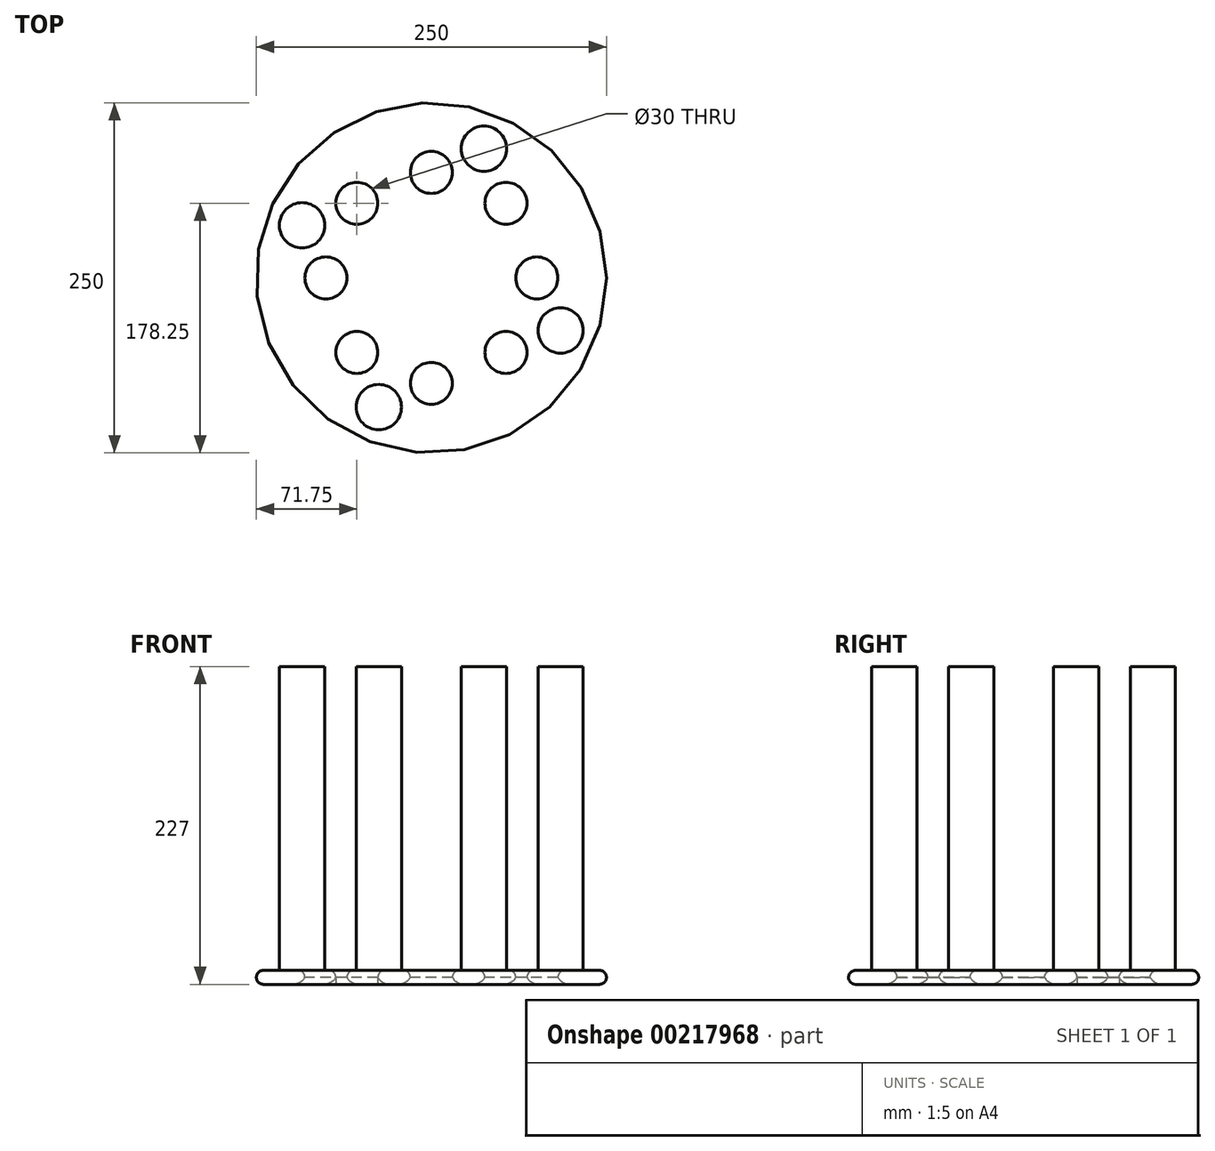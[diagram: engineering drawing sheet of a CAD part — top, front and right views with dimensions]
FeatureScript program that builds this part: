
annotation { "Feature Type Name" : "Feature", "Feature Type Description" : "" }
export const myFeature = defineFeature(function(context is Context, id is Id, definition is map)
    precondition{}
    {
        {
            var Q0;
            Q0=qCreatedBy(makeId("Top.planeOp"),FACE);
            var sketch = newSketch(context, id + "F0", { "sketchPlane" : qUnion([Q0])});
            skCircle(sketch, "E0", {"center": v(0, 0) * mm, "radius": 125 * mm});
            skCircle(sketch, "E1", {"center": v(0, 75.3) * mm, "radius": 15 * mm});
            skCircle(sketch, "E2.1.0", {"center": v(-53.25, 53.25) * mm, "radius": 15 * mm});
            skCircle(sketch, "E2.2.0", {"center": v(-75.3, 0) * mm, "radius": 15 * mm});
            skCircle(sketch, "E2.3.0", {"center": v(-53.25, -53.25) * mm, "radius": 15 * mm});
            skCircle(sketch, "E2.4.0", {"center": v(0, -75.3) * mm, "radius": 15 * mm});
            skCircle(sketch, "E2.5.0", {"center": v(53.25, -53.25) * mm, "radius": 15 * mm});
            skCircle(sketch, "E2.6.0", {"center": v(75.3, 0) * mm, "radius": 15 * mm});
            skCircle(sketch, "E2.7.0", {"center": v(53.25, 53.25) * mm, "radius": 15 * mm});
            skSolve(sketch);
        }
        {
            var Q0;
            Q0=makeQuery(id+"F0.imprint","IMPRINT",FACE,{"disambiguationData":[TD([[makeQuery(id+"F0.imprint","IMPRINT",EDGE,{"derivedFrom":sQuery(id+"F0.wireOp",EDGE,"E0")}),1.0]])]});
            extrude(context, id + "F1", {"entities" : qUnion([Q0]), "depth" : 10 * mm});
        }
        {
            var Q0;
            Q0=makeQuery(id+"F1.opExtrude","CAP_FACE",FACE,{"disambiguationData":[OSD([sQuery(id+"F0.wireOp",EDGE,"E0"),sQuery(id+"F0.wireOp",EDGE,"E1"),sQuery(id+"F0.wireOp",EDGE,"E2.1.0"),sQuery(id+"F0.wireOp",EDGE,"E2.2.0"),sQuery(id+"F0.wireOp",EDGE,"E2.3.0"),sQuery(id+"F0.wireOp",EDGE,"E2.4.0"),sQuery(id+"F0.wireOp",EDGE,"E2.5.0"),sQuery(id+"F0.wireOp",EDGE,"E2.6.0"),sQuery(id+"F0.wireOp",EDGE,"E2.7.0")])],"isStart":false});
            var Q1;
            Q1=makeQuery(id+"F1.opExtrude","SWEPT_FACE",FACE,{"disambiguationData":[OSD([sQuery(id+"F0.wireOp",EDGE,"E0")])]});
            fillet(context, id + "F2", {"entities" : qUnion([Q0, Q1]), "radius" : 5 * mm, "tangentPropagation" : true, "allowEdgeOverflow" : false});
        }
        {
            var Q0;
            {var subQ0=sQuery(id+"F0.wireOp",EDGE,"E0");Q0=makeQuery(id+"F2.opFillet","BLEND_EDGE",EDGE,{"blendedFrom":[makeQuery(id+"F1.opExtrude","CAP_EDGE",EDGE,{"disambiguationData":[OSD([subQ0])],"isStart":true}),makeQuery(id+"F1.opExtrude","CAP_FACE",FACE,{"disambiguationData":[OSD([subQ0,sQuery(id+"F0.wireOp",EDGE,"E1"),sQuery(id+"F0.wireOp",EDGE,"E2.1.0"),sQuery(id+"F0.wireOp",EDGE,"E2.2.0"),sQuery(id+"F0.wireOp",EDGE,"E2.3.0"),sQuery(id+"F0.wireOp",EDGE,"E2.4.0"),sQuery(id+"F0.wireOp",EDGE,"E2.5.0"),sQuery(id+"F0.wireOp",EDGE,"E2.6.0"),sQuery(id+"F0.wireOp",EDGE,"E2.7.0")])],"isStart":true})],"blendedInto":[makeQuery(id+"F1.opExtrude","CAP_FACE",FACE,{"disambiguationData":[OSD([subQ0,sQuery(id+"F0.wireOp",EDGE,"E1"),sQuery(id+"F0.wireOp",EDGE,"E2.1.0"),sQuery(id+"F0.wireOp",EDGE,"E2.2.0"),sQuery(id+"F0.wireOp",EDGE,"E2.3.0"),sQuery(id+"F0.wireOp",EDGE,"E2.4.0"),sQuery(id+"F0.wireOp",EDGE,"E2.5.0"),sQuery(id+"F0.wireOp",EDGE,"E2.6.0"),sQuery(id+"F0.wireOp",EDGE,"E2.7.0")])],"isStart":true})]});}
            var Q1;
            {var subQ0=sQuery(id+"F0.wireOp",EDGE,"E2.1.0");Q1=makeQuery(id+"F2.opFillet","BLEND_EDGE",EDGE,{"blendedFrom":[makeQuery(id+"F1.opExtrude","CAP_EDGE",EDGE,{"disambiguationData":[OSD([subQ0])],"isStart":false}),makeQuery(id+"F1.opExtrude","SWEPT_FACE",FACE,{"disambiguationData":[OSD([subQ0])]})],"blendedInto":[makeQuery(id+"F1.opExtrude","SWEPT_FACE",FACE,{"disambiguationData":[OSD([subQ0])]})]});}
            var Q2;
            Q2=makeQuery(id+"F1.opExtrude","CAP_EDGE",EDGE,{"disambiguationData":[OSD([sQuery(id+"F0.wireOp",EDGE,"E2.2.0")])],"isStart":true});
            var Q3;
            Q3=makeQuery(id+"F1.opExtrude","CAP_EDGE",EDGE,{"disambiguationData":[OSD([sQuery(id+"F0.wireOp",EDGE,"E2.3.0")])],"isStart":true});
            var Q4;
            Q4=makeQuery(id+"F1.opExtrude","CAP_EDGE",EDGE,{"disambiguationData":[OSD([sQuery(id+"F0.wireOp",EDGE,"E2.4.0")])],"isStart":true});
            var Q5;
            {var subQ0=sQuery(id+"F0.wireOp",EDGE,"E2.5.0");Q5=makeQuery(id+"F2.opFillet","BLEND_EDGE",EDGE,{"blendedFrom":[makeQuery(id+"F1.opExtrude","CAP_EDGE",EDGE,{"disambiguationData":[OSD([subQ0])],"isStart":false}),makeQuery(id+"F1.opExtrude","SWEPT_FACE",FACE,{"disambiguationData":[OSD([subQ0])]})],"blendedInto":[makeQuery(id+"F1.opExtrude","SWEPT_FACE",FACE,{"disambiguationData":[OSD([subQ0])]})]});}
            var Q6;
            Q6=makeQuery(id+"F1.opExtrude","CAP_EDGE",EDGE,{"disambiguationData":[OSD([sQuery(id+"F0.wireOp",EDGE,"E2.5.0")])],"isStart":true});
            var Q7;
            Q7=makeQuery(id+"F1.opExtrude","CAP_EDGE",EDGE,{"disambiguationData":[OSD([sQuery(id+"F0.wireOp",EDGE,"E1")])],"isStart":true});
            var Q8;
            Q8=makeQuery(id+"F1.opExtrude","CAP_EDGE",EDGE,{"disambiguationData":[OSD([sQuery(id+"F0.wireOp",EDGE,"E2.7.0")])],"isStart":true});
            var Q9;
            Q9=makeQuery(id+"F1.opExtrude","CAP_EDGE",EDGE,{"disambiguationData":[OSD([sQuery(id+"F0.wireOp",EDGE,"E2.6.0")])],"isStart":true});
            var Q10;
            {var subQ0=sQuery(id+"F0.wireOp",EDGE,"E2.6.0");Q10=makeQuery(id+"F2.opFillet","BLEND_EDGE",EDGE,{"blendedFrom":[makeQuery(id+"F1.opExtrude","CAP_EDGE",EDGE,{"disambiguationData":[OSD([subQ0])],"isStart":false}),makeQuery(id+"F1.opExtrude","CAP_FACE",FACE,{"disambiguationData":[OSD([sQuery(id+"F0.wireOp",EDGE,"E0"),sQuery(id+"F0.wireOp",EDGE,"E1"),sQuery(id+"F0.wireOp",EDGE,"E2.1.0"),sQuery(id+"F0.wireOp",EDGE,"E2.2.0"),sQuery(id+"F0.wireOp",EDGE,"E2.3.0"),sQuery(id+"F0.wireOp",EDGE,"E2.4.0"),sQuery(id+"F0.wireOp",EDGE,"E2.5.0"),subQ0,sQuery(id+"F0.wireOp",EDGE,"E2.7.0")])],"isStart":false})],"blendedInto":[makeQuery(id+"F1.opExtrude","CAP_FACE",FACE,{"disambiguationData":[OSD([sQuery(id+"F0.wireOp",EDGE,"E0"),sQuery(id+"F0.wireOp",EDGE,"E1"),sQuery(id+"F0.wireOp",EDGE,"E2.1.0"),sQuery(id+"F0.wireOp",EDGE,"E2.2.0"),sQuery(id+"F0.wireOp",EDGE,"E2.3.0"),sQuery(id+"F0.wireOp",EDGE,"E2.4.0"),sQuery(id+"F0.wireOp",EDGE,"E2.5.0"),subQ0,sQuery(id+"F0.wireOp",EDGE,"E2.7.0")])],"isStart":false})]});}
            var Q11;
            {var subQ0=sQuery(id+"F0.wireOp",EDGE,"E2.7.0");Q11=makeQuery(id+"F2.opFillet","BLEND_EDGE",EDGE,{"blendedFrom":[makeQuery(id+"F1.opExtrude","CAP_EDGE",EDGE,{"disambiguationData":[OSD([subQ0])],"isStart":false}),makeQuery(id+"F1.opExtrude","CAP_FACE",FACE,{"disambiguationData":[OSD([sQuery(id+"F0.wireOp",EDGE,"E0"),sQuery(id+"F0.wireOp",EDGE,"E1"),sQuery(id+"F0.wireOp",EDGE,"E2.1.0"),sQuery(id+"F0.wireOp",EDGE,"E2.2.0"),sQuery(id+"F0.wireOp",EDGE,"E2.3.0"),sQuery(id+"F0.wireOp",EDGE,"E2.4.0"),sQuery(id+"F0.wireOp",EDGE,"E2.5.0"),sQuery(id+"F0.wireOp",EDGE,"E2.6.0"),subQ0])],"isStart":false})],"blendedInto":[makeQuery(id+"F1.opExtrude","CAP_FACE",FACE,{"disambiguationData":[OSD([sQuery(id+"F0.wireOp",EDGE,"E0"),sQuery(id+"F0.wireOp",EDGE,"E1"),sQuery(id+"F0.wireOp",EDGE,"E2.1.0"),sQuery(id+"F0.wireOp",EDGE,"E2.2.0"),sQuery(id+"F0.wireOp",EDGE,"E2.3.0"),sQuery(id+"F0.wireOp",EDGE,"E2.4.0"),sQuery(id+"F0.wireOp",EDGE,"E2.5.0"),sQuery(id+"F0.wireOp",EDGE,"E2.6.0"),subQ0])],"isStart":false})]});}
            var Q12;
            {var subQ0=sQuery(id+"F0.wireOp",EDGE,"E1");Q12=makeQuery(id+"F2.opFillet","BLEND_EDGE",EDGE,{"blendedFrom":[makeQuery(id+"F1.opExtrude","CAP_EDGE",EDGE,{"disambiguationData":[OSD([subQ0])],"isStart":false}),makeQuery(id+"F1.opExtrude","CAP_FACE",FACE,{"disambiguationData":[OSD([sQuery(id+"F0.wireOp",EDGE,"E0"),subQ0,sQuery(id+"F0.wireOp",EDGE,"E2.1.0"),sQuery(id+"F0.wireOp",EDGE,"E2.2.0"),sQuery(id+"F0.wireOp",EDGE,"E2.3.0"),sQuery(id+"F0.wireOp",EDGE,"E2.4.0"),sQuery(id+"F0.wireOp",EDGE,"E2.5.0"),sQuery(id+"F0.wireOp",EDGE,"E2.6.0"),sQuery(id+"F0.wireOp",EDGE,"E2.7.0")])],"isStart":false})],"blendedInto":[makeQuery(id+"F1.opExtrude","CAP_FACE",FACE,{"disambiguationData":[OSD([sQuery(id+"F0.wireOp",EDGE,"E0"),subQ0,sQuery(id+"F0.wireOp",EDGE,"E2.1.0"),sQuery(id+"F0.wireOp",EDGE,"E2.2.0"),sQuery(id+"F0.wireOp",EDGE,"E2.3.0"),sQuery(id+"F0.wireOp",EDGE,"E2.4.0"),sQuery(id+"F0.wireOp",EDGE,"E2.5.0"),sQuery(id+"F0.wireOp",EDGE,"E2.6.0"),sQuery(id+"F0.wireOp",EDGE,"E2.7.0")])],"isStart":false})]});}
            var Q13;
            {var subQ0=sQuery(id+"F0.wireOp",EDGE,"E2.1.0");Q13=makeQuery(id+"F2.opFillet","BLEND_EDGE",EDGE,{"blendedFrom":[makeQuery(id+"F1.opExtrude","CAP_EDGE",EDGE,{"disambiguationData":[OSD([subQ0])],"isStart":false}),makeQuery(id+"F1.opExtrude","CAP_FACE",FACE,{"disambiguationData":[OSD([sQuery(id+"F0.wireOp",EDGE,"E0"),sQuery(id+"F0.wireOp",EDGE,"E1"),subQ0,sQuery(id+"F0.wireOp",EDGE,"E2.2.0"),sQuery(id+"F0.wireOp",EDGE,"E2.3.0"),sQuery(id+"F0.wireOp",EDGE,"E2.4.0"),sQuery(id+"F0.wireOp",EDGE,"E2.5.0"),sQuery(id+"F0.wireOp",EDGE,"E2.6.0"),sQuery(id+"F0.wireOp",EDGE,"E2.7.0")])],"isStart":false})],"blendedInto":[makeQuery(id+"F1.opExtrude","CAP_FACE",FACE,{"disambiguationData":[OSD([sQuery(id+"F0.wireOp",EDGE,"E0"),sQuery(id+"F0.wireOp",EDGE,"E1"),subQ0,sQuery(id+"F0.wireOp",EDGE,"E2.2.0"),sQuery(id+"F0.wireOp",EDGE,"E2.3.0"),sQuery(id+"F0.wireOp",EDGE,"E2.4.0"),sQuery(id+"F0.wireOp",EDGE,"E2.5.0"),sQuery(id+"F0.wireOp",EDGE,"E2.6.0"),sQuery(id+"F0.wireOp",EDGE,"E2.7.0")])],"isStart":false})]});}
            var Q14;
            {var subQ0=sQuery(id+"F0.wireOp",EDGE,"E2.2.0");Q14=makeQuery(id+"F2.opFillet","BLEND_EDGE",EDGE,{"blendedFrom":[makeQuery(id+"F1.opExtrude","CAP_EDGE",EDGE,{"disambiguationData":[OSD([subQ0])],"isStart":false}),makeQuery(id+"F1.opExtrude","CAP_FACE",FACE,{"disambiguationData":[OSD([sQuery(id+"F0.wireOp",EDGE,"E0"),sQuery(id+"F0.wireOp",EDGE,"E1"),sQuery(id+"F0.wireOp",EDGE,"E2.1.0"),subQ0,sQuery(id+"F0.wireOp",EDGE,"E2.3.0"),sQuery(id+"F0.wireOp",EDGE,"E2.4.0"),sQuery(id+"F0.wireOp",EDGE,"E2.5.0"),sQuery(id+"F0.wireOp",EDGE,"E2.6.0"),sQuery(id+"F0.wireOp",EDGE,"E2.7.0")])],"isStart":false})],"blendedInto":[makeQuery(id+"F1.opExtrude","CAP_FACE",FACE,{"disambiguationData":[OSD([sQuery(id+"F0.wireOp",EDGE,"E0"),sQuery(id+"F0.wireOp",EDGE,"E1"),sQuery(id+"F0.wireOp",EDGE,"E2.1.0"),subQ0,sQuery(id+"F0.wireOp",EDGE,"E2.3.0"),sQuery(id+"F0.wireOp",EDGE,"E2.4.0"),sQuery(id+"F0.wireOp",EDGE,"E2.5.0"),sQuery(id+"F0.wireOp",EDGE,"E2.6.0"),sQuery(id+"F0.wireOp",EDGE,"E2.7.0")])],"isStart":false})]});}
            var Q15;
            {var subQ0=sQuery(id+"F0.wireOp",EDGE,"E2.3.0");Q15=makeQuery(id+"F2.opFillet","BLEND_EDGE",EDGE,{"blendedFrom":[makeQuery(id+"F1.opExtrude","CAP_EDGE",EDGE,{"disambiguationData":[OSD([subQ0])],"isStart":false}),makeQuery(id+"F1.opExtrude","SWEPT_FACE",FACE,{"disambiguationData":[OSD([subQ0])]})],"blendedInto":[makeQuery(id+"F1.opExtrude","SWEPT_FACE",FACE,{"disambiguationData":[OSD([subQ0])]})]});}
            var Q16;
            {var subQ0=sQuery(id+"F0.wireOp",EDGE,"E2.3.0");Q16=makeQuery(id+"F2.opFillet","BLEND_EDGE",EDGE,{"blendedFrom":[makeQuery(id+"F1.opExtrude","CAP_EDGE",EDGE,{"disambiguationData":[OSD([subQ0])],"isStart":false}),makeQuery(id+"F1.opExtrude","CAP_FACE",FACE,{"disambiguationData":[OSD([sQuery(id+"F0.wireOp",EDGE,"E0"),sQuery(id+"F0.wireOp",EDGE,"E1"),sQuery(id+"F0.wireOp",EDGE,"E2.1.0"),sQuery(id+"F0.wireOp",EDGE,"E2.2.0"),subQ0,sQuery(id+"F0.wireOp",EDGE,"E2.4.0"),sQuery(id+"F0.wireOp",EDGE,"E2.5.0"),sQuery(id+"F0.wireOp",EDGE,"E2.6.0"),sQuery(id+"F0.wireOp",EDGE,"E2.7.0")])],"isStart":false})],"blendedInto":[makeQuery(id+"F1.opExtrude","CAP_FACE",FACE,{"disambiguationData":[OSD([sQuery(id+"F0.wireOp",EDGE,"E0"),sQuery(id+"F0.wireOp",EDGE,"E1"),sQuery(id+"F0.wireOp",EDGE,"E2.1.0"),sQuery(id+"F0.wireOp",EDGE,"E2.2.0"),subQ0,sQuery(id+"F0.wireOp",EDGE,"E2.4.0"),sQuery(id+"F0.wireOp",EDGE,"E2.5.0"),sQuery(id+"F0.wireOp",EDGE,"E2.6.0"),sQuery(id+"F0.wireOp",EDGE,"E2.7.0")])],"isStart":false})]});}
            var Q17;
            {var subQ0=sQuery(id+"F0.wireOp",EDGE,"E2.4.0");Q17=makeQuery(id+"F2.opFillet","BLEND_EDGE",EDGE,{"blendedFrom":[makeQuery(id+"F1.opExtrude","CAP_EDGE",EDGE,{"disambiguationData":[OSD([subQ0])],"isStart":false}),makeQuery(id+"F1.opExtrude","CAP_FACE",FACE,{"disambiguationData":[OSD([sQuery(id+"F0.wireOp",EDGE,"E0"),sQuery(id+"F0.wireOp",EDGE,"E1"),sQuery(id+"F0.wireOp",EDGE,"E2.1.0"),sQuery(id+"F0.wireOp",EDGE,"E2.2.0"),sQuery(id+"F0.wireOp",EDGE,"E2.3.0"),subQ0,sQuery(id+"F0.wireOp",EDGE,"E2.5.0"),sQuery(id+"F0.wireOp",EDGE,"E2.6.0"),sQuery(id+"F0.wireOp",EDGE,"E2.7.0")])],"isStart":false})],"blendedInto":[makeQuery(id+"F1.opExtrude","CAP_FACE",FACE,{"disambiguationData":[OSD([sQuery(id+"F0.wireOp",EDGE,"E0"),sQuery(id+"F0.wireOp",EDGE,"E1"),sQuery(id+"F0.wireOp",EDGE,"E2.1.0"),sQuery(id+"F0.wireOp",EDGE,"E2.2.0"),sQuery(id+"F0.wireOp",EDGE,"E2.3.0"),subQ0,sQuery(id+"F0.wireOp",EDGE,"E2.5.0"),sQuery(id+"F0.wireOp",EDGE,"E2.6.0"),sQuery(id+"F0.wireOp",EDGE,"E2.7.0")])],"isStart":false})]});}
            var Q18;
            {var subQ0=sQuery(id+"F0.wireOp",EDGE,"E2.5.0");Q18=makeQuery(id+"F2.opFillet","BLEND_EDGE",EDGE,{"blendedFrom":[makeQuery(id+"F1.opExtrude","CAP_EDGE",EDGE,{"disambiguationData":[OSD([subQ0])],"isStart":false}),makeQuery(id+"F1.opExtrude","CAP_FACE",FACE,{"disambiguationData":[OSD([sQuery(id+"F0.wireOp",EDGE,"E0"),sQuery(id+"F0.wireOp",EDGE,"E1"),sQuery(id+"F0.wireOp",EDGE,"E2.1.0"),sQuery(id+"F0.wireOp",EDGE,"E2.2.0"),sQuery(id+"F0.wireOp",EDGE,"E2.3.0"),sQuery(id+"F0.wireOp",EDGE,"E2.4.0"),subQ0,sQuery(id+"F0.wireOp",EDGE,"E2.6.0"),sQuery(id+"F0.wireOp",EDGE,"E2.7.0")])],"isStart":false})],"blendedInto":[makeQuery(id+"F1.opExtrude","CAP_FACE",FACE,{"disambiguationData":[OSD([sQuery(id+"F0.wireOp",EDGE,"E0"),sQuery(id+"F0.wireOp",EDGE,"E1"),sQuery(id+"F0.wireOp",EDGE,"E2.1.0"),sQuery(id+"F0.wireOp",EDGE,"E2.2.0"),sQuery(id+"F0.wireOp",EDGE,"E2.3.0"),sQuery(id+"F0.wireOp",EDGE,"E2.4.0"),subQ0,sQuery(id+"F0.wireOp",EDGE,"E2.6.0"),sQuery(id+"F0.wireOp",EDGE,"E2.7.0")])],"isStart":false})]});}
            fillet(context, id + "F3", {"entities" : qUnion([Q0, Q1, Q2, Q3, Q4, Q5, Q6, Q7, Q8, Q9, Q10, Q11, Q12, Q13, Q14, Q15, Q16, Q17, Q18]), "radius" : 10 * mm, "tangentPropagation" : true, "allowEdgeOverflow" : false});
        }
        {
            var Q0;
            Q0=makeQuery(id+"F1.opExtrude","CAP_FACE",FACE,{"disambiguationData":[OSD([sQuery(id+"F0.wireOp",EDGE,"E0"),sQuery(id+"F0.wireOp",EDGE,"E1"),sQuery(id+"F0.wireOp",EDGE,"E2.1.0"),sQuery(id+"F0.wireOp",EDGE,"E2.2.0"),sQuery(id+"F0.wireOp",EDGE,"E2.3.0"),sQuery(id+"F0.wireOp",EDGE,"E2.4.0"),sQuery(id+"F0.wireOp",EDGE,"E2.5.0"),sQuery(id+"F0.wireOp",EDGE,"E2.6.0"),sQuery(id+"F0.wireOp",EDGE,"E2.7.0")])],"isStart":false});
            var sketch = newSketch(context, id + "F4", { "sketchPlane" : qUnion([Q0])});
            skCircle(sketch, "E3", {"center": v(-92.28, 37.53) * mm, "radius": 16.18 * mm});
            skCircle(sketch, "E4.1.0", {"center": v(-37.53, -92.28) * mm, "radius": 16.18 * mm});
            skCircle(sketch, "E4.2.0", {"center": v(92.28, -37.53) * mm, "radius": 16.18 * mm});
            skCircle(sketch, "E4.3.0", {"center": v(37.53, 92.28) * mm, "radius": 16.18 * mm});
            skPoint(sketch, "E4.center", {"position": v(0, 0) * mm});
            skSolve(sketch);
        }
        {
            var Q0;
            Q0=makeQuery(id+"F4.imprint","IMPRINT",FACE,{"disambiguationData":[TD([[makeQuery(id+"F4.imprint","IMPRINT",EDGE,{"derivedFrom":sQuery(id+"F4.wireOp",EDGE,"E3")}),1.0]])]});
            var Q1;
            Q1=makeQuery(id+"F4.imprint","IMPRINT",FACE,{"disambiguationData":[TD([[makeQuery(id+"F4.imprint","IMPRINT",EDGE,{"derivedFrom":sQuery(id+"F4.wireOp",EDGE,"E4.3.0")}),1.0]])]});
            var Q2;
            Q2=makeQuery(id+"F4.imprint","IMPRINT",FACE,{"disambiguationData":[TD([[makeQuery(id+"F4.imprint","IMPRINT",EDGE,{"derivedFrom":sQuery(id+"F4.wireOp",EDGE,"E4.2.0")}),1.0]])]});
            var Q3;
            Q3=makeQuery(id+"F4.imprint","IMPRINT",FACE,{"disambiguationData":[TD([[makeQuery(id+"F4.imprint","IMPRINT",EDGE,{"derivedFrom":sQuery(id+"F4.wireOp",EDGE,"E4.1.0")}),1.0]])]});
            extrude(context, id + "F5", {"entities" : qUnion([Q0, Q1, Q2, Q3]), "operationType" : NewBodyOperationType.ADD, "depth" : 25 * mm});
        }
        {
            var Q0;
            Q0=makeQuery(id+"F5.opExtrude","CAP_FACE",FACE,{"disambiguationData":[OSD([sQuery(id+"F4.wireOp",EDGE,"E3")])],"isStart":false});
            var Q1;
            Q1=makeQuery(id+"F5.opExtrude","CAP_FACE",FACE,{"disambiguationData":[OSD([sQuery(id+"F4.wireOp",EDGE,"E4.3.0")])],"isStart":false});
            var Q2;
            Q2=makeQuery(id+"F5.opExtrude","CAP_FACE",FACE,{"disambiguationData":[OSD([sQuery(id+"F4.wireOp",EDGE,"E4.2.0")])],"isStart":false});
            var Q3;
            Q3=makeQuery(id+"F5.opExtrude","CAP_FACE",FACE,{"disambiguationData":[OSD([sQuery(id+"F4.wireOp",EDGE,"E4.1.0")])],"isStart":false});
            extrude(context, id + "F6", {"entities" : qUnion([Q0, Q1, Q2, Q3]), "operationType" : NewBodyOperationType.ADD, "depth" : 192 * mm});
        }
    });
